# Revit family: 1Manifold FHF-F_2-12_TWA-A_RFA
name_source: partatom
category: Pipe Accessories
units: mm (PartAtom-declared; Revit-internal decimal feet)

## family parameters
Always vertical = Yes
Cut with Voids When Loaded = No
OmniClass Number = 23.65.55.14.17
OmniClass Title = Adjusting/Controlling Valves for Liquid Services
Part Type = Normal
Round Connector Dimension = Use Diameter
Shared = No
Work Plane-Based = No

## types (11) — shared parameters
088H3106 = TWA-A_RFA : TWA-A_230V_NC/S_0.95m_088H3106
088H3112 = TWA-A_RFA : TWA-A_230V_NC_0.95m_088H3112
088H3113 = TWA-A_RFA : TWA-A_230V_NO_0.95m_088H3113
088H3118 = TWA-A_RFA : TWA-A_230V_NC_5m_088H3118
088H3119 = TWA-A_RFA : TWA-A_230V_NC_10m_088H3119
088U0785 = _FHF-EA_EM : FHF-EA_088U0785
088U0786 = _FHF-EA_EM : FHF-EM_088U0786
Actuator Type = TWA-A_RFA : TWA-A_230V_NC_0.95m_088H3112
D = 25 mm  [stored 0.082021 ft]
Description = Brass Manifold
H1 = 73 mm
H2 = 38 mm  [stored 0.124672 ft]
IfcExportAs = IfcValveType
IfcExportType = FHF-F
LOD 200 = No
LOD 350 = Yes
Manufacturer = Danfoss
Max Differential Pressure = 0.6 bar
Max Operating Pressure = 6 bar
Max Working Temperature = 90 °C
URL = https://store.danfoss.com
Valve Body Material = Danfoss Brass
Voltage = 230 V

## per-type parameters (varying)
| type | L | L bracket | L1 | Length | Model | Model Type | Number of Circuits | Power |
| Manifold FHF-F_2+2_088U0522 | 170 mm  [stored 0.557743 ft] | 50 mm  [stored 0.164042 ft] | 111 mm | 100 mm  [stored 0.328084 ft] | 088U0522 | Manifold FHF-F_2+2 | 2 | 4 VA |
| Manifold FHF-F_12+12_088U0532 | 670 mm  [stored 2.19816 ft] | 550 mm | 611 mm  [stored 2.00459 ft] | 600 mm | 088U0532 | Manifold FHF-F_12+12 | 12 | 24 VA |
| Manifold FHF-F_3+3_088U0523 | 220 mm  [stored 0.721785 ft] | 100 mm  [stored 0.328084 ft] | 161 mm  [stored 0.528215 ft] | 150 mm | 088U0523 | Manifold FHF-F_3+3 | 3 | 6 VA |
| Manifold FHF-F_4+4_088U0524 | 270 mm  [stored 0.885827 ft] | 150 mm | 211 mm  [stored 0.692257 ft] | 200 mm  [stored 0.656168 ft] | 088U0524 | Manifold FHF-F_4+4 | 4 | 8 VA |
| Manifold FHF-F_5+5_088U0525 | 320 mm  [stored 1.04987 ft] | 200 mm  [stored 0.656168 ft] | 261 mm | 250 mm  [stored 0.82021 ft] | 088U0525 | Manifold FHF-F_5+5 | 5 | 10 VA |
| Manifold FHF-F_6+6_088U0526 | 370 mm  [stored 1.21391 ft] | 250 mm  [stored 0.82021 ft] | 311 mm  [stored 1.02034 ft] | 300 mm  [stored 0.984252 ft] | 088U0526 | Manifold FHF-F_6+6 | 6 | 12 VA |
| Manifold FHF-F_7+7_088U0527 | 420 mm  [stored 1.37795 ft] | 300 mm  [stored 0.984252 ft] | 361 mm  [stored 1.18438 ft] | 350 mm  [stored 1.14829 ft] | 088U0527 | Manifold FHF-F_7+7 | 7 | 14 VA |
| Manifold FHF-F_8+8_088U0528 | 470 mm  [stored 1.54199 ft] | 350 mm  [stored 1.14829 ft] | 411 mm  [stored 1.34843 ft] | 400 mm  [stored 1.31234 ft] | 088U0528 | Manifold FHF-F_8+8 | 8 | 16 VA |
| Manifold FHF-F_9+9_088U0529 | 520 mm  [stored 1.70604 ft] | 400 mm  [stored 1.31234 ft] | 461 mm  [stored 1.51247 ft] | 450 mm  [stored 1.47638 ft] | 088U0529 | Manifold FHF-F_9+9 | 9 | 18 VA |
| Manifold FHF-F_10+10_088U0530 | 570 mm  [stored 1.87008 ft] | 450 mm  [stored 1.47638 ft] | 511 mm | 500 mm  [stored 1.64042 ft] | 088U0530 | Manifold FHF-F_10+10 | 10 | 20 VA |
| Manifold FHF-F_11+11_088U0531 | 620 mm | 500 mm  [stored 1.64042 ft] | 561 mm | 550 mm | 088U0531 | Manifold FHF-F_11+11 | 11 | 22 VA |

note: [stored X ft] marks values corroborated as IEEE doubles in the binary element streams (Revit-internal decimal feet)

## geometry (parser evidence)
native form markers: Blend x2, Sweep x13
no freeform markers — native parametric forms only
